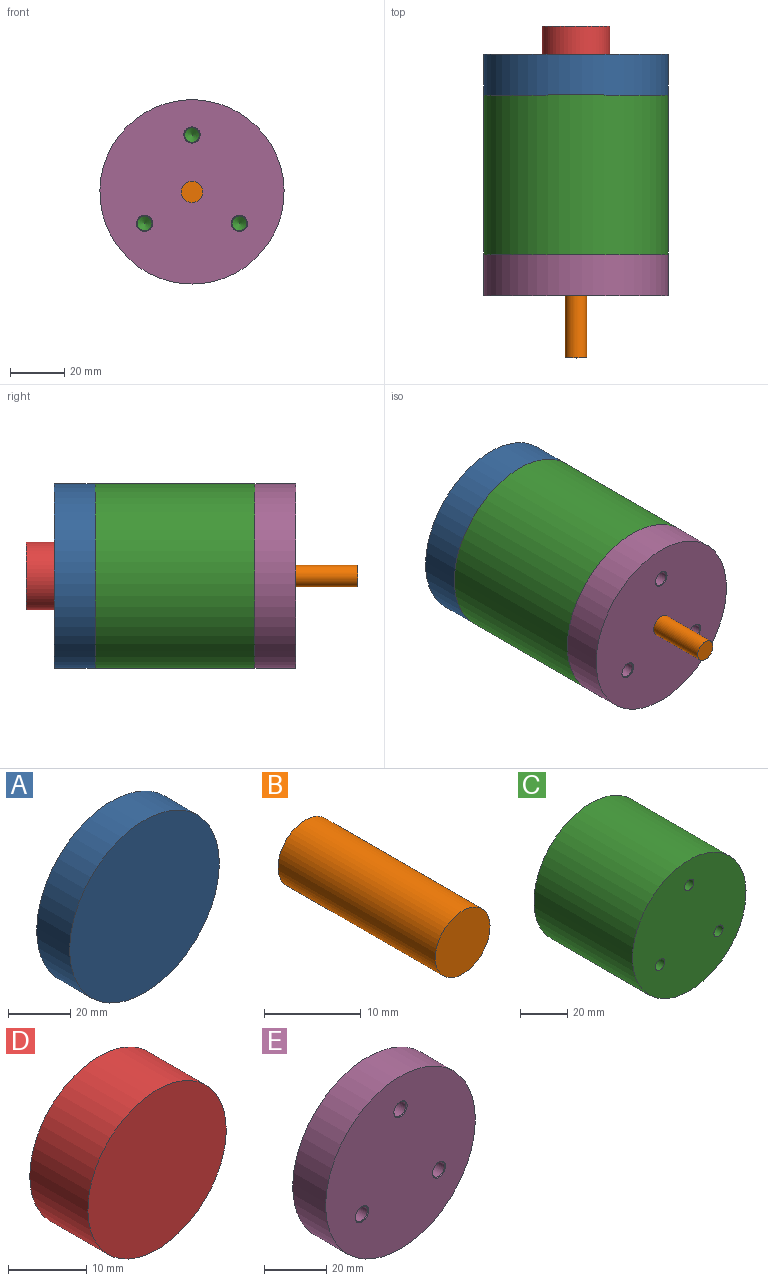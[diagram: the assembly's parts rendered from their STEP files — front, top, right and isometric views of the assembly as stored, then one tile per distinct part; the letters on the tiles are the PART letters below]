
ASSEMBLY  parts=5 mates=4
PART A: 3 faces, bbox 68x15x68 mm
  f0: cylinder r=34mm len=68mm, axis (0,-1,0), area 3204.4mm2, adj f1,f2
  f1: plane 68x68mm, normal (0,1,0), area 3631.7mm2, adj f0
  f2: plane 68x68mm, normal (0,-1,0), area 3631.7mm2, adj f0
PART B: 3 faces, bbox 8x23x8 mm
  f0: cylinder r=4mm len=23mm, axis (0,1,0), area 578.1mm2, adj f1,f2
  f1: plane 8x8mm, normal (0,-1,0), area 50.3mm2, adj f0
  f2: plane 8x8mm, normal (0,1,0), area 50.3mm2, adj f0
PART C: 9 faces, bbox 68x59x68 mm
  f0: cylinder r=34mm len=68mm, axis (0,-1,0), area 12604.1mm2, adj f1,f2
  f1: plane 68x68mm, normal (0,1,0), area 3631.7mm2, adj f0
  f2: plane 68x68mm, normal (0,-1,0), area 3560.4mm2, adj f0,f3,f5,f7
  f3: cylinder r=2.75mm len=35mm, axis (0,-1,0), area 604.8mm2, adj f2,f4
  f4: cone r=0mm half-angle=59deg, axis (0,-1,0), area 27.7mm2, adj f3
  f5: cylinder r=2.75mm len=35mm, axis (0,-1,0), area 604.8mm2, adj f2,f6
  f6: cone r=0mm half-angle=59deg, axis (0,-1,0), area 27.7mm2, adj f5
  f7: cylinder r=2.75mm len=35mm, axis (0,-1,0), area 604.8mm2, adj f2,f8
  f8: cone r=0mm half-angle=59deg, axis (0,-1,0), area 27.7mm2, adj f7
PART D: 3 faces, bbox 25x10.5x25 mm
  f0: cylinder r=12.5mm len=25mm, axis (0,-1,0), area 824.7mm2, adj f1,f2
  f1: plane 25x25mm, normal (0,1,0), area 490.9mm2, adj f0
  f2: plane 25x25mm, normal (0,-1,0), area 490.9mm2, adj f0
PART E: 9 faces, bbox 68x15x68 mm
  f0: cylinder r=34mm len=68mm, axis (0,1,0), area 3204.4mm2, adj f1,f2
  f1: plane 68x68mm, normal (0,-1,0), area 3546.9mm2, adj f0,f4,f6,f8
  f2: plane 68x68mm, normal (0,1,0), area 3560.4mm2, adj f0,f3,f5,f7
  f3: cylinder r=2.75mm len=14.75mm, axis (0,-1,0), area 254.9mm2, adj f2,f4
  f4: cone r=2.75mm half-angle=45deg, axis (0,-1,0), area 6.4mm2, adj f1,f3
  f5: cylinder r=2.75mm len=14.75mm, axis (0,-1,0), area 254.9mm2, adj f2,f6
  f6: cone r=2.75mm half-angle=45deg, axis (0,-1,0), area 6.4mm2, adj f1,f5
  f7: cylinder r=2.75mm len=14.75mm, axis (0,-1,0), area 254.9mm2, adj f2,f8
  f8: cone r=2.75mm half-angle=45deg, axis (0,-1,0), area 6.4mm2, adj f1,f7
PLACE A t=(28.29,-108.72,-25.49)mm
PLACE B t=(28.29,-108.72,-25.48)mm
PLACE C t=(28.29,-108.72,-25.49)mm
PLACE D t=(28.29,-108.72,-25.49)mm
PLACE E t=(28.29,-108.72,-25.49)mm
MATE fastened B.f0 <-> E.f1  axis (0,1,0) through (28.29,-123.72,-25.48)mm
MATE fastened A.f0 <-> C.f0  axis (0,-1,0) through (28.29,-49.72,-25.49)mm
MATE fastened E.f0 <-> C.f0  axis (0,1,0) through (28.29,-108.72,-25.49)mm
MATE fastened D.f0 <-> A.f0  axis (0,-1,0) through (28.29,-34.72,-25.49)mm
